# Revit family: CADS_AIRFLOWdev_AirTerminal_Cowl_GravityFlapIntake
name_source: partatom
category: Air Terminals
revit_build: Autodesk Revit 2015 (Build: 20160512_0715(x64)
units: mm (PartAtom-declared; Revit-internal decimal feet)

## types (3) — shared parameters
6MonthlyMaintenance = Visually inspect system, clean the fan and ducting if necessary
AirflowRateRange = 0-61
AssetType = Fixed
C = 10 mm  [stored 0.0328084 ft]
CEApproval = Yes
Color = Silver
Constituents = Silver
Cowl_GravityFlap = CADS_Airflow_Chrome
D = 10 mm  [stored 0.0328084 ft]
Default Elevation = 1219 mm
DurationUnit = Years
Exclusions = Incorrect Use / Incorrect Installation / Installed by a non-accredited electrician. Customer abuse.
FaceType = LOUVERED
Grade = Virgin
HasIntegralControl = No
HasSoundAttenuator = No
HasThermalInsulation = No
ISO140001 = Yes
ISO90001 = Yes
IsExtendedWarranty = No
Manufacturer = Airflow Developments Ltd
ManufacturerAddress = Aidelle House
Lancaster Road
Cressex Business Park
High Wycombe
Bucks
HP123QP
ManufacturerTelephone = 01494 525252
ManufacturerWebsite = www.airflow.com
Material = Stainless Steel
MountingType = SURFACE
NBSCode = 90-75-50/370 Air terminals;
PointOfContact = Airflow Developments Ltd
ProductionYear = 2017
ServiceLifeDuration = 10
ServiceLifeType = EXPECTEDSERVICELIFE
Uniclass2015 = Pr_65_70_46_01
WarrantyContent = Replacement of part if faulty
WarrantyGuarantor = Airflow Developments Ltd
WarrantyPeriod = 2
zero-valued in all types: NumberOfSlots

## per-type parameters (varying)
| type | A | B | Description | E | F | FlowControlType | G | GlobalTradeItemNumber | GrossWeight | ModelLabel | ModelReference | NominalHeight | NominalLength | NominalWidth | ReplacementCost | Shape | ShippingWeight | Size |
| 125 | 125 mm  [stored 0.410105 ft] | 50 mm  [stored 0.164042 ft] | 125mm dia square cowl complete with gravity flap | 67 mm | 20 mm  [stored 0.0656168 ft] | DAMPER | 180 mm  [stored 0.590551 ft] | 5019009318059 | 0.05 kg | 125mm dia square cowl complete with gravity flap | 9041230 | 184 mm  [stored 0.603675 ft] | 95 mm | 184 mm  [stored 0.603675 ft] | 38.184 | Rectangular | 0.05 kg | 95 x 184 x 184 |
| 150 | 150 mm | 55 mm  [stored 0.180446 ft] | 150mm dia square cowl complete with gravity flap | 70 mm  [stored 0.229659 ft] | 18 mm  [stored 0.0590551 ft] | DAMPER | 184 mm  [stored 0.603675 ft] | 5019009306438 | 0.06 kg | 150mm dia square cowl complete with gravity flap | 9041231 | 184 mm  [stored 0.603675 ft] | 98 mm  [stored 0.321522 ft] | 184 mm  [stored 0.603675 ft] | 44.544 | Rectangular | 0.07 kg | 98 x 184 x 184 |
| 160 | 160 mm  [stored 0.524934 ft] | 55 mm  [stored 0.180446 ft] | 160mm dia round cowl complete with internal mesh | 70 mm  [stored 0.229659 ft] | 18 mm  [stored 0.0590551 ft] | NONE | 184 mm  [stored 0.603675 ft] | 5019009318714 | 0.07 kg | 160mm dia round cowl complete with internal mesh | 90000506 | 210 mm  [stored 0.688976 ft] | 165 mm | 210 mm  [stored 0.688976 ft] | 48.468 | Round | 0.08 kg | 165 x 210 x 210 |

note: [stored X ft] marks values corroborated as IEEE doubles in the binary element streams (Revit-internal decimal feet)

## geometry (parser evidence)
native form markers: Blend x10, Sweep x2
no freeform markers — native parametric forms only
